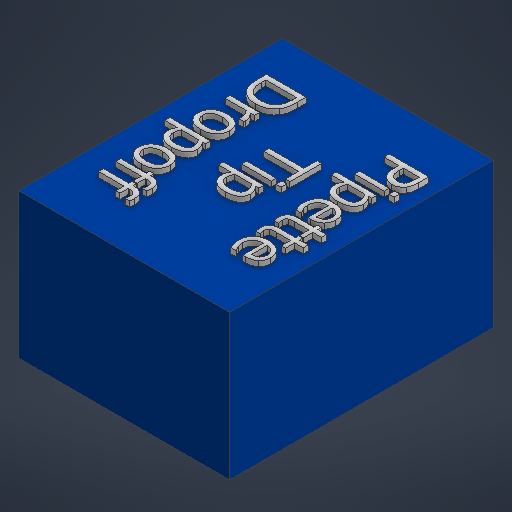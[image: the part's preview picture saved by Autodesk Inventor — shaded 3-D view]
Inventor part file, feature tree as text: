
AUTODESK INVENTOR PART (.ipt)
format: ipt  version: 2025.1 (Build 291241000, 241)  size: 522,240 bytes
history: native  units: mm
features: extrude x2, sketch x2
ambient origin geometry x8: Origin, YZ Plane, XZ Plane, XY Plane, X Axis, Y Axis, Z Axis, Center Point
bodies: Solid1 (feature_tree)
feature tree (4):
  extrude  "Extrusion1"  Depth=100.0mm
  extrude  "Extrusion2"  Depth=2.0mm TaperAngle=0.0deg
  sketch  "Sketch1"  dims[d0=80.0mm d1=100.0mm]
  sketch  "Sketch2"  dims[d2=55.0mm d3=0.0mm d4=2.0mm d5=0.0mm]
